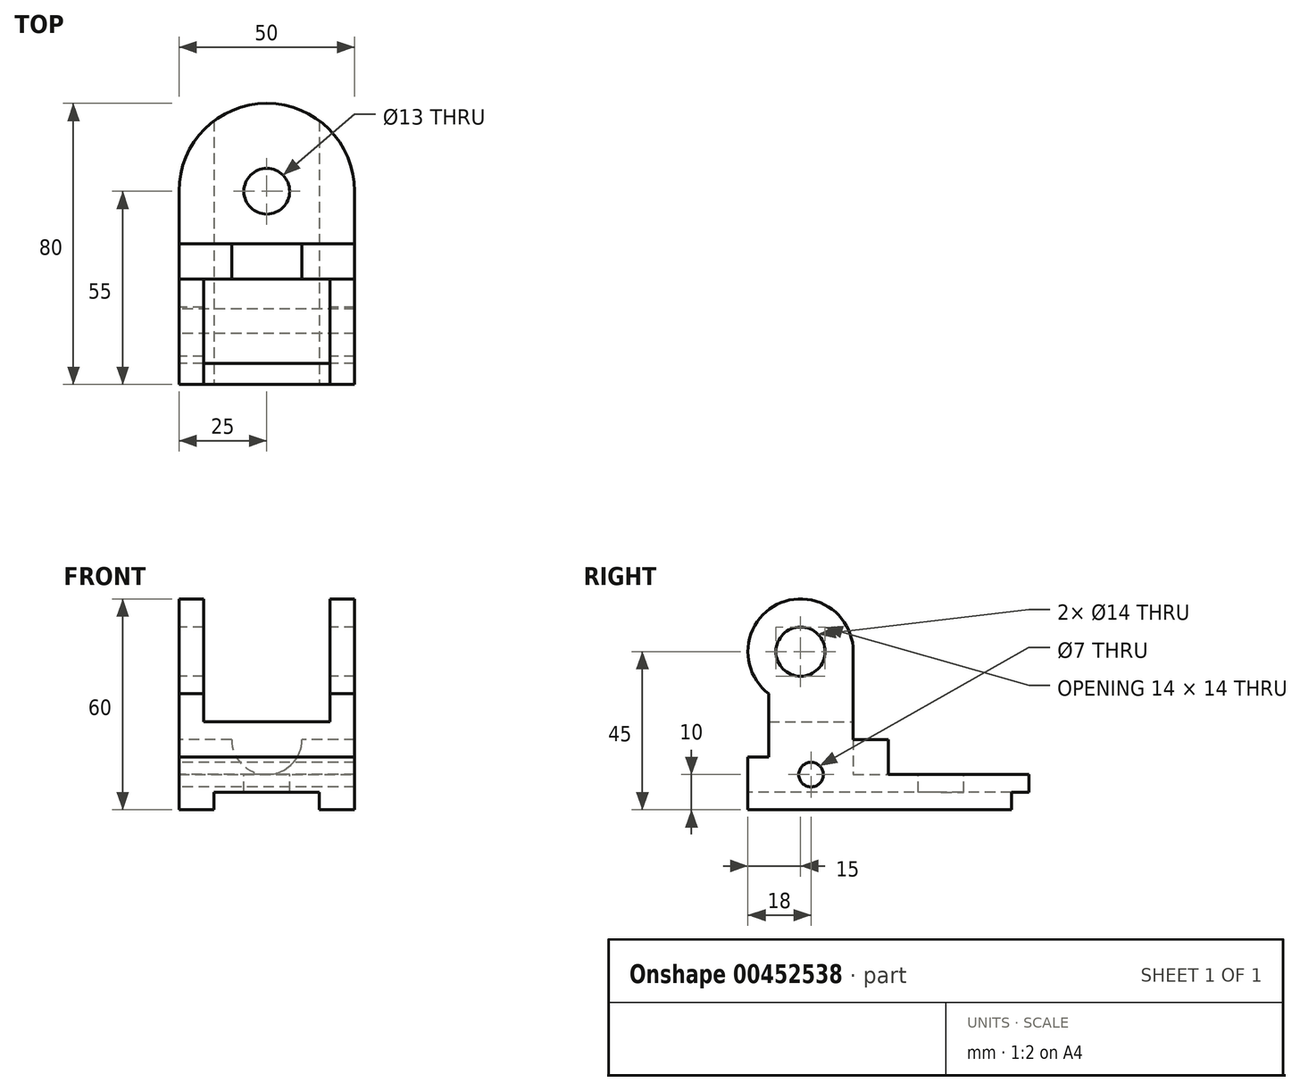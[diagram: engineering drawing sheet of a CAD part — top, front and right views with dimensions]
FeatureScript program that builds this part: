
annotation { "Feature Type Name" : "Feature", "Feature Type Description" : "" }
export const myFeature = defineFeature(function(context is Context, id is Id, definition is map)
    precondition{}
    {
        {
            var Q0;
            Q0=qCreatedBy(makeId("Right.planeOp"),FACE);
            var sketch = newSketch(context, id + "F0", { "sketchPlane" : qUnion([Q0])});
            skLineSegment(sketch, "E0", {"start": v(0, 0) * mm, "end": v(0, 15) * mm});
            skLineSegment(sketch, "E1", {"start": v(0, 15) * mm, "end": v(6, 15) * mm});
            skLineSegment(sketch, "E2", {"start": v(6, 15) * mm, "end": v(6, 33) * mm});
            skLineSegment(sketch, "E3", {"start": v(0, 0) * mm, "end": v(55, 0) * mm});
            skLineSegment(sketch, "E4", {"start": v(55, 0) * mm, "end": v(55, 10) * mm});
            skLineSegment(sketch, "E5", {"start": v(55, 10) * mm, "end": v(30, 10) * mm});
            skLineSegment(sketch, "E6", {"start": v(30, 10) * mm, "end": v(30, 45) * mm});
            skArc(sketch, "E7", {"start": v(30, 45) * mm, "mid": v(8.3, 58.42) * mm, "end": v(6, 33) * mm});
            skCircle(sketch, "E8", {"center": v(15, 45) * mm, "radius": 7 * mm});
            skCircle(sketch, "E9", {"center": v(18, 10) * mm, "radius": 3.5 * mm});
            skSolve(sketch);
        }
        {
            var Q0;
            Q0=makeQuery(id+"F0.imprint","IMPRINT",FACE,{"disambiguationData":[TD([[makeQuery(id+"F0.imprint","IMPRINT",EDGE,{"derivedFrom":sQuery(id+"F0.wireOp",EDGE,"E0")}),-1.0]])]});
            extrude(context, id + "F1", {"entities" : qUnion([Q0]), "endBound" : BoundingType.SYMMETRIC, "depth" : 50 * mm});
        }
        {
            var Q0;
            Q0=makeQuery(id+"F1.opExtrude","SWEPT_FACE",FACE,{"disambiguationData":[OSD([sQuery(id+"F0.wireOp",EDGE,"E3")])]});
            var sketch = newSketch(context, id + "F2", { "sketchPlane" : qUnion([Q0])});
            skArc(sketch, "E10", {"start": v(-25, -55) * mm, "mid": v(0, -80) * mm, "end": v(25, -55) * mm});
            skSolve(sketch);
        }
        {
            var Q0;
            Q0=makeQuery(id+"F2.imprint","IMPRINT",FACE,{"disambiguationData":[TD([[makeQuery(id+"F2.imprint","IMPRINT",EDGE,{"derivedFrom":sQuery(id+"F2.wireOp",EDGE,"E10")}),1.0]])]});
            extrude(context, id + "F3", {"entities" : qUnion([Q0]), "operationType" : NewBodyOperationType.ADD, "oppositeDirection" : true, "depth" : 10 * mm});
        }
        {
            var Q0;
            Q0=makeQuery(id+"F3.boolean.opBoolean","MERGE",FACE,{"derivedFrom":[makeQuery(id+"F1.opExtrude","SWEPT_FACE",FACE,{"disambiguationData":[OSD([sQuery(id+"F0.wireOp",EDGE,"E5")])]}),makeQuery(id+"F3.opExtrude","CAP_FACE",FACE,{"disambiguationData":[OSD([sQuery(id+"F0.wireOp",EDGE,"E3"),sQuery(id+"F0.wireOp",EDGE,"E4"),sQuery(id+"F2.wireOp",EDGE,"E10")])],"isStart":false})]});
            var sketch = newSketch(context, id + "F4", { "sketchPlane" : qUnion([Q0])});
            skCircle(sketch, "E11", {"center": v(0, 55) * mm, "radius": 6.5 * mm});
            skSolve(sketch);
        }
        {
            var Q0;
            Q0=sQuery(id+"F4.wireOp",VERTEX,"E11.center");
            var Q1;
            Q1=makeQuery(id+"F1.opExtrude","SWEPT_BODY",BODY,{"disambiguationData":[OSD([sQuery(id+"F0.wireOp",EDGE,"E0"),sQuery(id+"F0.wireOp",EDGE,"E1"),sQuery(id+"F0.wireOp",EDGE,"E2"),sQuery(id+"F0.wireOp",EDGE,"E3"),sQuery(id+"F0.wireOp",EDGE,"E4"),sQuery(id+"F0.wireOp",EDGE,"E5"),sQuery(id+"F0.wireOp",EDGE,"E6"),sQuery(id+"F0.wireOp",EDGE,"E7"),sQuery(id+"F0.wireOp",EDGE,"E8"),sQuery(id+"F0.wireOp",EDGE,"E9")])]});
            hole(context, id + "F5", {"style" : HoleStyle.SIMPLE, "endStyle" : HoleEndStyle.THROUGH, "holeDiameter" : 13 * mm, "isTappedThrough" : true, "tappedDepth" : 12 * mm, "tapClearance" : 3, "locations" : qUnion([Q0]), "scope" : qUnion([Q1])});
        }
        {
            var Q0;
            Q0=makeQuery(id+"F1.opExtrude","SWEPT_FACE",FACE,{"disambiguationData":[OSD([sQuery(id+"F0.wireOp",EDGE,"E6")])]});
            var sketch = newSketch(context, id + "F6", { "sketchPlane" : qUnion([Q0])});
            skLineSegment(sketch, "E12.bottom", {"start": v(18, 25) * mm, "end": v(-18, 25) * mm});
            skLineSegment(sketch, "E12.top", {"start": v(18, 60) * mm, "end": v(-18, 60) * mm});
            skLineSegment(sketch, "E12.left", {"start": v(18, 25) * mm, "end": v(18, 60) * mm});
            skLineSegment(sketch, "E12.right", {"start": v(-18, 25) * mm, "end": v(-18, 60) * mm});
            skPoint(sketch, "E12.middle", {"position": v(0, 42.5) * mm});
            skSolve(sketch);
        }
        {
            var Q0;
            {var subQ0=sQuery(id+"F6.wireOp",EDGE,"E12.top");Q0=makeQuery(id+"F6.imprint","IMPRINT",FACE,{"disambiguationData":[TD([[makeQuery(id+"F6.imprint","IMPRINT",EDGE,{"derivedFrom":subQ0}),1.0]])]});}
            var Q1;
            {var subQ0=sQuery(id+"F6.wireOp",EDGE,"E12.bottom");Q1=makeQuery(id+"F6.imprint","IMPRINT",FACE,{"disambiguationData":[TD([[makeQuery(id+"F6.imprint","IMPRINT",EDGE,{"derivedFrom":subQ0}),-1.0]])]});}
            extrude(context, id + "F7", {"entities" : qUnion([Q0, Q1]), "operationType" : NewBodyOperationType.REMOVE, "endBound" : BoundingType.THROUGH_ALL, "oppositeDirection" : true, "depth" : 52.2 * mm});
        }
        {
            var Q0;
            Q0=makeQuery(id+"F1.opExtrude","SWEPT_FACE",FACE,{"disambiguationData":[OSD([sQuery(id+"F0.wireOp",EDGE,"E0")])]});
            var sketch = newSketch(context, id + "F8", { "sketchPlane" : qUnion([Q0])});
            skLineSegment(sketch, "E13.bottom", {"start": v(-15, 5) * mm, "end": v(15, 5) * mm});
            skLineSegment(sketch, "E13.top", {"start": v(-15, -5) * mm, "end": v(15, -5) * mm});
            skLineSegment(sketch, "E13.left", {"start": v(-15, 5) * mm, "end": v(-15, -5) * mm});
            skLineSegment(sketch, "E13.right", {"start": v(15, 5) * mm, "end": v(15, -5) * mm});
            skPoint(sketch, "E13.middle", {"position": v(0, 0) * mm});
            skSolve(sketch);
        }
        {
            var Q0;
            {var subQ0=sQuery(id+"F8.wireOp",EDGE,"E13.bottom");Q0=makeQuery(id+"F8.imprint","IMPRINT",FACE,{"disambiguationData":[TD([[makeQuery(id+"F8.imprint","IMPRINT",EDGE,{"derivedFrom":subQ0}),-1.0]])]});}
            var Q1;
            {var subQ0=sQuery(id+"F8.wireOp",EDGE,"E13.top");Q1=makeQuery(id+"F8.imprint","IMPRINT",FACE,{"disambiguationData":[TD([[makeQuery(id+"F8.imprint","IMPRINT",EDGE,{"derivedFrom":subQ0}),1.0]])]});}
            extrude(context, id + "F9", {"entities" : qUnion([Q0, Q1]), "operationType" : NewBodyOperationType.REMOVE, "endBound" : BoundingType.THROUGH_ALL, "oppositeDirection" : true, "depth" : 25 * mm});
        }
        {
            var Q0;
            Q0=makeQuery(id+"F1.opExtrude","SWEPT_FACE",FACE,{"disambiguationData":[OSD([sQuery(id+"F0.wireOp",EDGE,"E6")])]});
            var sketch = newSketch(context, id + "F10", { "sketchPlane" : qUnion([Q0])});
            skLineSegment(sketch, "E14", {"start": v(-25, 10) * mm, "end": v(-25, 20) * mm});
            skLineSegment(sketch, "E15", {"start": v(-25, 20) * mm, "end": v(25, 20) * mm});
            skLineSegment(sketch, "E16", {"start": v(25, 20) * mm, "end": v(25, 10) * mm});
            skLineSegment(sketch, "E17", {"start": v(25, 10) * mm, "end": v(-25, 10) * mm});
            skSolve(sketch);
        }
        {
            var Q0;
            Q0=makeQuery(id+"F10.imprint","IMPRINT",FACE,{"disambiguationData":[TD([[makeQuery(id+"F10.imprint","IMPRINT",EDGE,{"derivedFrom":sQuery(id+"F10.wireOp",EDGE,"E14")}),-1.0]])]});
            extrude(context, id + "F11", {"entities" : qUnion([Q0]), "operationType" : NewBodyOperationType.ADD, "depth" : 10 * mm});
        }
        {
            var Q0;
            Q0=makeQuery(id+"F11.opExtrude","CAP_FACE",FACE,{"disambiguationData":[OSD([sQuery(id+"F10.wireOp",EDGE,"E14"),sQuery(id+"F10.wireOp",EDGE,"E15"),sQuery(id+"F10.wireOp",EDGE,"E16"),sQuery(id+"F10.wireOp",EDGE,"E17")])],"isStart":false});
            var sketch = newSketch(context, id + "F12", { "sketchPlane" : qUnion([Q0])});
            skCircle(sketch, "E18", {"center": v(0, 20) * mm, "radius": 10 * mm});
            skSolve(sketch);
        }
        {
            var Q0;
            {var subQ0=sQuery(id+"F12.wireOp",EDGE,"E18");var subQ1=makeQuery(id+"F11.opExtrude","CAP_EDGE",EDGE,{"disambiguationData":[OSD([sQuery(id+"F10.wireOp",EDGE,"E15")])],"isStart":false});var subQ2=makeQuery(id+"F12.imprint","INTERSECT",VERTEX,{"disambiguationData":[OD(0.0)],"derivedFrom":[subQ1,subQ0]});Q0=makeQuery(id+"F12.imprint","IMPRINT",FACE,{"disambiguationData":[TD([[makeQuery(id+"F12.imprint","IMPRINT",EDGE,{"disambiguationData":[TD([[subQ2,-1.0]])],"derivedFrom":subQ0}),1.0]])]});}
            var Q1;
            Q1=sQuery(id+"F12.wireOp",EDGE,"E18");
            extrude(context, id + "F13", {"entities" : qUnion([Q0]), "operationType" : NewBodyOperationType.REMOVE, "surfaceEntities" : qUnion([Q1]), "oppositeDirection" : true, "depth" : 10 * mm});
        }
    });
